FCSTD DOCUMENT  (FreeCAD 0.16R6706 (Git))
Label: test
License: All rights reserved
LicenseURL: http://en.wikipedia.org/wiki/All_rights_reserved
objects: Sketcher::SketchObject×2, Spreadsheet::Sheet×1
note: 2 computed .brp shape members not serialized (recipe doc carries the construction recipe); baked Part::Feature solids carry a one-line shape summary decoded from their .brp

FEATURE [Sketcher::SketchObject] Sketch  label="uShape"
  expr: Constraints[17] = prefs.height
  expr: Constraints[21] = prefs.u
  expr: Constraints[20] = prefs.width
  sketch-geometry (8):
    g0: LineSegment StartX=100 StartY=100 StartZ=0 EndX=100 EndY=0 EndZ=0
    g1: LineSegment StartX=100 StartY=0 StartZ=0 EndX=0 EndY=0 EndZ=0
    g2: LineSegment StartX=0 StartY=0 StartZ=0 EndX=0 EndY=100 EndZ=0
    g3: LineSegment StartX=0 StartY=100 StartZ=0 EndX=33.3333 EndY=100 EndZ=0
    g4: LineSegment StartX=33.3333 StartY=100 StartZ=0 EndX=33.3333 EndY=50 EndZ=0
    g5: LineSegment StartX=33.3333 StartY=50 StartZ=0 EndX=66.6667 EndY=50 EndZ=0
    g6: LineSegment StartX=66.6667 StartY=50 StartZ=0 EndX=66.6667 EndY=100 EndZ=0
    g7: LineSegment StartX=66.6667 StartY=100 StartZ=0 EndX=100 EndY=100 EndZ=0
  constraints (24):
    c: Vertical(g0)
    c: Coincident(g0,g1)
    c: Horizontal(g1)
    c: Coincident(g1,g2)
    c: Vertical(g2)
    c: Coincident(g2,g3)
    c: Coincident(g3,g4)
    c: Vertical(g4)
    c: Coincident(g4,g5)
    c: Coincident(g5,g6)
    c: Vertical(g6)
    c: Coincident(g6,g7)
    c: Coincident(g7,g0)
    c: Horizontal(g7)
    c: Horizontal(g3)
    c: Equal(g7,g5)
    c: Equal(g3,g5)
    c: DistanceY(g0,g0) = 100
    c: Equal(g0,g2)
    c: Equal(g6,g4)
    c: DistanceX(g1,g0) = 100
    c: DistanceY(g5,g6) = 50
    c: DistanceX(g1,g-1) = 0
    c: DistanceY(g1,g-1) = 0
FEATURE [Spreadsheet::Sheet] Spreadsheet  label="prefs"
  cells = A2=height; B2(height)=100; C2=mm; A3=width; B3(width)=100; C3=mm; A4=u; B4(u)=50; C4=mm; A5=space; B5(space)=10; C5=mm
FEATURE [Sketcher::SketchObject] Sketch001  label="uShape001"
  Placement = pos=(0,110,0) rot=(0,0,1;0rad)
  expr: Constraints[17] = prefs.height
  expr: Placement.Base.y = prefs.height + prefs.space
  expr: Constraints[21] = prefs.u
  expr: Constraints[20] = prefs.width
  sketch-geometry (8):
    g0: LineSegment StartX=100 StartY=100 StartZ=0 EndX=100 EndY=0 EndZ=0
    g1: LineSegment StartX=100 StartY=0 StartZ=0 EndX=0 EndY=0 EndZ=0
    g2: LineSegment StartX=0 StartY=0 StartZ=0 EndX=0 EndY=100 EndZ=0
    g3: LineSegment StartX=0 StartY=100 StartZ=0 EndX=33.3333 EndY=100 EndZ=0
    g4: LineSegment StartX=33.3333 StartY=100 StartZ=0 EndX=33.3333 EndY=50 EndZ=0
    g5: LineSegment StartX=33.3333 StartY=50 StartZ=0 EndX=66.6667 EndY=50 EndZ=0
    g6: LineSegment StartX=66.6667 StartY=50 StartZ=0 EndX=66.6667 EndY=100 EndZ=0
    g7: LineSegment StartX=66.6667 StartY=100 StartZ=0 EndX=100 EndY=100 EndZ=0
  constraints (24):
    c: Vertical(g0)
    c: Coincident(g0,g1)
    c: Horizontal(g1)
    c: Coincident(g1,g2)
    c: Vertical(g2)
    c: Coincident(g2,g3)
    c: Coincident(g3,g4)
    c: Vertical(g4)
    c: Coincident(g4,g5)
    c: Coincident(g5,g6)
    c: Vertical(g6)
    c: Coincident(g6,g7)
    c: Coincident(g7,g0)
    c: Horizontal(g7)
    c: Horizontal(g3)
    c: Equal(g7,g5)
    c: Equal(g3,g5)
    c: DistanceY(g0,g0) = 100
    c: Equal(g0,g2)
    c: Equal(g6,g4)
    c: DistanceX(g1,g0) = 100
    c: DistanceY(g5,g6) = 50
    c: DistanceX(g1,g-1) = 0
    c: DistanceY(g1,g-1) = 0
